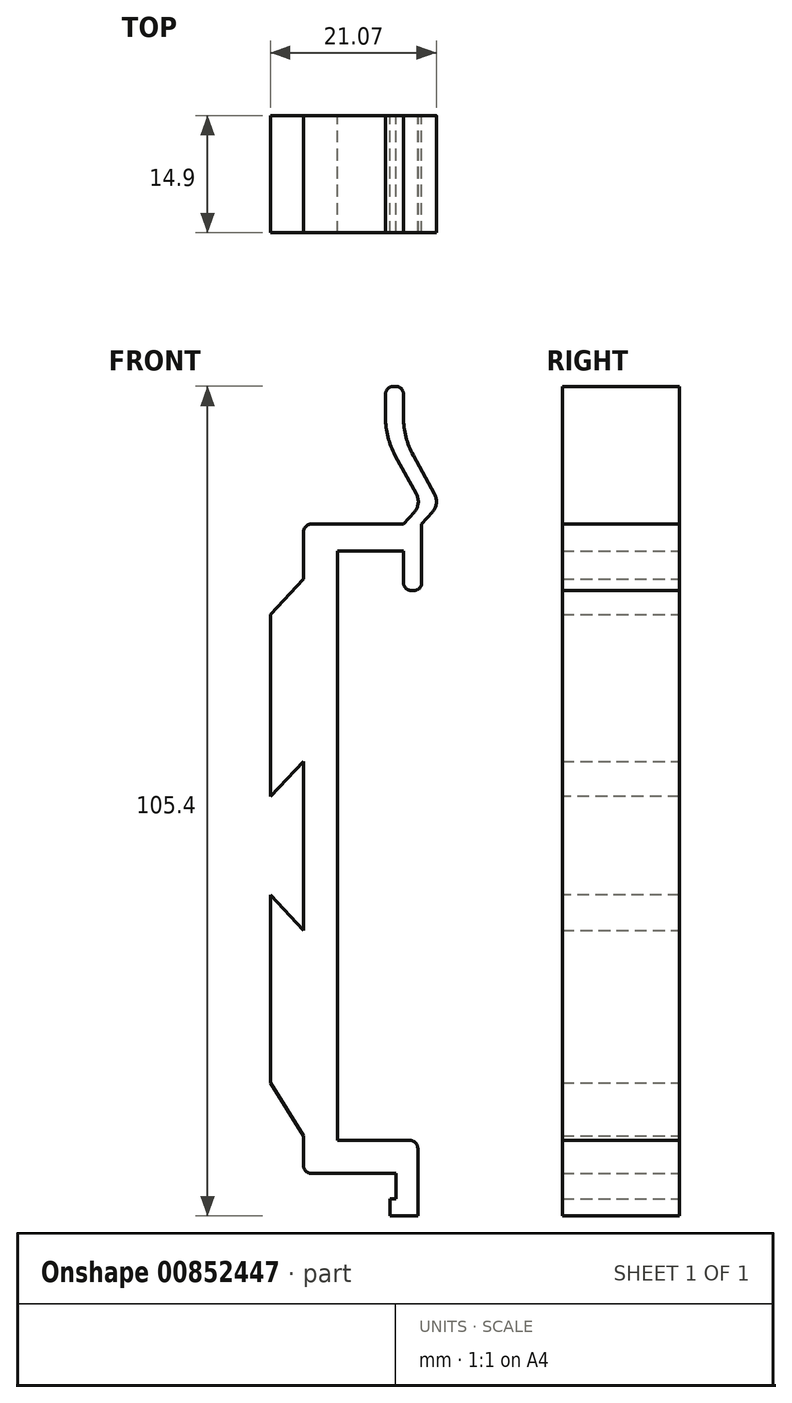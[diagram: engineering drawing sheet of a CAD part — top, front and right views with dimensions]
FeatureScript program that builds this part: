
annotation { "Feature Type Name" : "Feature", "Feature Type Description" : "" }
export const myFeature = defineFeature(function(context is Context, id is Id, definition is map)
    precondition{}
    {
        {
            var Q0;
            Q0=qCreatedBy(makeId("Front.planeOp"),FACE);
            var sketch = newSketch(context, id + "F0", { "sketchPlane" : qUnion([Q0])});
            skLineSegment(sketch, "E0", {"start": v(-4.3, -36.83) * mm, "end": v(-8.5, -30.1) * mm});
            skLineSegment(sketch, "E1", {"start": v(-8.5, -30.1) * mm, "end": v(-8.5, 6.6) * mm});
            skLineSegment(sketch, "E2", {"start": v(-8.5, 6.6) * mm, "end": v(-18.45, 13.87) * mm});
            skLineSegment(sketch, "E3", {"start": v(-18.45, 13.87) * mm, "end": v(-18.45, 27.37) * mm});
            skLineSegment(sketch, "E4", {"start": v(-16.45, 29.37) * mm, "end": v(-13.95, 29.37) * mm});
            skLineSegment(sketch, "E5", {"start": v(-13.95, 29.38) * mm, "end": v(-13.95, 20.08) * mm});
            skLineSegment(sketch, "E6", {"start": v(-13.95, 20.07) * mm, "end": v(-8.5, 20.08) * mm});
            skLineSegment(sketch, "E7", {"start": v(-8.5, 20.08) * mm, "end": v(-8.5, 29.38) * mm});
            skLineSegment(sketch, "E8", {"start": v(-8.5, 29.37) * mm, "end": v(-4.3, 33.87) * mm});
            skLineSegment(sketch, "E9", {"start": v(-4.3, 33.87) * mm, "end": v(-4.3, 39.88) * mm});
            skLineSegment(sketch, "E10", {"start": v(-3.3, 40.88) * mm, "end": v(8.4, 40.88) * mm});
            skLineSegment(sketch, "E11", {"start": v(10.7, 40.88) * mm, "end": v(10.7, 33.43) * mm});
            skLineSegment(sketch, "E12", {"start": v(9.7, 32.43) * mm, "end": v(9.4, 32.43) * mm});
            skLineSegment(sketch, "E13", {"start": v(8.4, 33.43) * mm, "end": v(8.4, 37.43) * mm});
            skLineSegment(sketch, "E14", {"start": v(8.4, 37.43) * mm, "end": v(0, 37.42) * mm});
            skLineSegment(sketch, "E15", {"start": v(0, 37.42) * mm, "end": v(0, -37.42) * mm});
            skLineSegment(sketch, "E16", {"start": v(0, -37.42) * mm, "end": v(9.2, -37.42) * mm});
            skLineSegment(sketch, "E17", {"start": v(10.2, -38.42) * mm, "end": v(10.2, -47.02) * mm});
            skLineSegment(sketch, "E18", {"start": v(10.2, -47.02) * mm, "end": v(6.7, -47.02) * mm});
            skLineSegment(sketch, "E19", {"start": v(6.7, -47.02) * mm, "end": v(6.7, -44.82) * mm});
            skLineSegment(sketch, "E20", {"start": v(6.7, -44.82) * mm, "end": v(7.45, -44.82) * mm});
            skLineSegment(sketch, "E21", {"start": v(7.45, -44.82) * mm, "end": v(7.45, -41.62) * mm});
            skLineSegment(sketch, "E22", {"start": v(7.45, -41.62) * mm, "end": v(-3.3, -41.62) * mm});
            skLineSegment(sketch, "E23", {"start": v(-4.3, -40.62) * mm, "end": v(-4.3, -36.83) * mm});
            skLineSegment(sketch, "E24", {"start": v(8.4, 57.38) * mm, "end": v(8.4, 54.41) * mm});
            skLineSegment(sketch, "E25", {"start": v(9.63, 49.61) * mm, "end": v(12.32, 44.69) * mm});
            skLineSegment(sketch, "E26", {"start": v(12.06, 42.4) * mm, "end": v(10.7, 40.87) * mm});
            skLineSegment(sketch, "E27", {"start": v(7.4, 58.38) * mm, "end": v(7.1, 58.38) * mm});
            skLineSegment(sketch, "E28", {"start": v(6.1, 57.38) * mm, "end": v(6.1, 54.41) * mm});
            skLineSegment(sketch, "E29", {"start": v(7.33, 49.61) * mm, "end": v(10.02, 44.69) * mm});
            skLineSegment(sketch, "E30", {"start": v(9.76, 42.4) * mm, "end": v(8.4, 40.88) * mm});
            skPoint(sketch, "E31.visualSharp", {"position": v(6.1, 51.86) * mm});
            skArc(sketch, "E31.filletArc", {"start": v(6.1, 54.41) * mm, "mid": v(6.41, 51.94) * mm, "end": v(7.33, 49.61) * mm});
            skPoint(sketch, "E32.visualSharp", {"position": v(8.4, 51.86) * mm});
            skArc(sketch, "E32.filletArc", {"start": v(8.4, 54.41) * mm, "mid": v(8.71, 51.94) * mm, "end": v(9.63, 49.61) * mm});
            skPoint(sketch, "E33.visualSharp", {"position": v(10.7, 43.45) * mm});
            skArc(sketch, "E33.filletArc", {"start": v(9.76, 42.4) * mm, "mid": v(10.25, 43.5) * mm, "end": v(10.02, 44.69) * mm});
            skPoint(sketch, "E34.visualSharp", {"position": v(13, 43.45) * mm});
            skArc(sketch, "E34.filletArc", {"start": v(12.06, 42.4) * mm, "mid": v(12.55, 43.5) * mm, "end": v(12.32, 44.69) * mm});
            skPoint(sketch, "E35.visualSharp", {"position": v(8.4, 58.38) * mm});
            skArc(sketch, "E35.filletArc", {"start": v(8.4, 57.38) * mm, "mid": v(8.1, 58.08) * mm, "end": v(7.4, 58.38) * mm});
            skPoint(sketch, "E36.visualSharp", {"position": v(6.1, 58.38) * mm});
            skArc(sketch, "E36.filletArc", {"start": v(7.1, 58.38) * mm, "mid": v(6.4, 58.08) * mm, "end": v(6.1, 57.38) * mm});
            skPoint(sketch, "E37.visualSharp", {"position": v(10.7, 32.43) * mm});
            skArc(sketch, "E37.filletArc", {"start": v(9.7, 32.43) * mm, "mid": v(10.4, 32.72) * mm, "end": v(10.7, 33.43) * mm});
            skPoint(sketch, "E38.visualSharp", {"position": v(8.4, 32.43) * mm});
            skArc(sketch, "E38.filletArc", {"start": v(8.4, 33.43) * mm, "mid": v(8.7, 32.72) * mm, "end": v(9.4, 32.43) * mm});
            skPoint(sketch, "E39.visualSharp", {"position": v(-4.3, 40.87) * mm});
            skArc(sketch, "E39.filletArc", {"start": v(-3.3, 40.88) * mm, "mid": v(-4, 40.58) * mm, "end": v(-4.3, 39.88) * mm});
            skPoint(sketch, "E40.visualSharp", {"position": v(-18.45, 29.37) * mm});
            skArc(sketch, "E40.filletArc", {"start": v(-16.45, 29.38) * mm, "mid": v(-17.86, 28.79) * mm, "end": v(-18.45, 27.37) * mm});
            skPoint(sketch, "E41.visualSharp", {"position": v(-4.3, -41.62) * mm});
            skArc(sketch, "E41.filletArc", {"start": v(-4.3, -40.62) * mm, "mid": v(-4, -41.33) * mm, "end": v(-3.3, -41.62) * mm});
            skPoint(sketch, "E42.visualSharp", {"position": v(10.2, -37.42) * mm});
            skArc(sketch, "E42.filletArc", {"start": v(10.2, -38.42) * mm, "mid": v(9.9, -37.72) * mm, "end": v(9.2, -37.42) * mm});
            skSolve(sketch);
        }
        {
            var Q0;
            Q0=qSketchRegion(id+"F0",true);
            extrude(context, id + "F1", {"entities" : qUnion([Q0]), "depth" : 14.9 * mm, "symmetric" : true});
        }
        {
            var Q0;
            Q0=makeQuery(id+"F1.opExtrude","CAP_FACE",FACE,{"disambiguationData":[OSD([sQuery(id+"F0.wireOp",EDGE,"E0"),sQuery(id+"F0.wireOp",EDGE,"E1"),sQuery(id+"F0.wireOp",EDGE,"E2"),sQuery(id+"F0.wireOp",EDGE,"E3"),sQuery(id+"F0.wireOp",EDGE,"E4"),sQuery(id+"F0.wireOp",EDGE,"E5"),sQuery(id+"F0.wireOp",EDGE,"E6"),sQuery(id+"F0.wireOp",EDGE,"E7"),sQuery(id+"F0.wireOp",EDGE,"E8"),sQuery(id+"F0.wireOp",EDGE,"E9"),sQuery(id+"F0.wireOp",EDGE,"E10"),sQuery(id+"F0.wireOp",EDGE,"E11"),sQuery(id+"F0.wireOp",EDGE,"E12"),sQuery(id+"F0.wireOp",EDGE,"E13"),sQuery(id+"F0.wireOp",EDGE,"E14"),sQuery(id+"F0.wireOp",EDGE,"E15"),sQuery(id+"F0.wireOp",EDGE,"E16"),sQuery(id+"F0.wireOp",EDGE,"E17"),sQuery(id+"F0.wireOp",EDGE,"E18"),sQuery(id+"F0.wireOp",EDGE,"E19"),sQuery(id+"F0.wireOp",EDGE,"E20"),sQuery(id+"F0.wireOp",EDGE,"E21"),sQuery(id+"F0.wireOp",EDGE,"E22"),sQuery(id+"F0.wireOp",EDGE,"E23"),sQuery(id+"F0.wireOp",EDGE,"E24"),sQuery(id+"F0.wireOp",EDGE,"E25"),sQuery(id+"F0.wireOp",EDGE,"E26"),sQuery(id+"F0.wireOp",EDGE,"E27"),sQuery(id+"F0.wireOp",EDGE,"E28"),sQuery(id+"F0.wireOp",EDGE,"E29"),sQuery(id+"F0.wireOp",EDGE,"E30"),sQuery(id+"F0.wireOp",EDGE,"E31.filletArc"),sQuery(id+"F0.wireOp",EDGE,"E32.filletArc"),sQuery(id+"F0.wireOp",EDGE,"E33.filletArc"),sQuery(id+"F0.wireOp",EDGE,"E34.filletArc"),sQuery(id+"F0.wireOp",EDGE,"E35.filletArc"),sQuery(id+"F0.wireOp",EDGE,"E36.filletArc"),sQuery(id+"F0.wireOp",EDGE,"E37.filletArc"),sQuery(id+"F0.wireOp",EDGE,"E38.filletArc"),sQuery(id+"F0.wireOp",EDGE,"E39.filletArc"),sQuery(id+"F0.wireOp",EDGE,"E40.filletArc"),sQuery(id+"F0.wireOp",EDGE,"E41.filletArc"),sQuery(id+"F0.wireOp",EDGE,"E42.filletArc")])],"isStart":false});
            var sketch = newSketch(context, id + "F2", { "sketchPlane" : qUnion([Q0])});
            skLineSegment(sketch, "E43.bottom", {"start": v(-18.45, 29.38) * mm, "end": v(-8.5, 29.38) * mm});
            skLineSegment(sketch, "E43.top", {"start": v(-18.45, -30.1) * mm, "end": v(-8.5, -30.1) * mm});
            skLineSegment(sketch, "E43.left", {"start": v(-18.45, 29.38) * mm, "end": v(-18.45, -30.1) * mm});
            skLineSegment(sketch, "E43.right", {"start": v(-8.5, 29.38) * mm, "end": v(-8.5, -30.1) * mm});
            skSolve(sketch);
        }
        {
            var Q0;
            Q0 = qSketchRegion(id + "F2", true);
            extrude(context, id + "F3", {"entities" : qUnion([Q0]), "operationType" : NewBodyOperationType.REMOVE, "endBound" : BoundingType.THROUGH_ALL, "oppositeDirection" : true, "depth" : 25 * mm, "offsetDistance" : 25 * mm});
        }
        {
            var Q0;
            Q0=makeQuery(id+"F1.opExtrude","CAP_FACE",FACE,{"disambiguationData":[OSD([sQuery(id+"F0.wireOp",EDGE,"E0"),sQuery(id+"F0.wireOp",EDGE,"E1"),sQuery(id+"F0.wireOp",EDGE,"E2"),sQuery(id+"F0.wireOp",EDGE,"E3"),sQuery(id+"F0.wireOp",EDGE,"E4"),sQuery(id+"F0.wireOp",EDGE,"E5"),sQuery(id+"F0.wireOp",EDGE,"E6"),sQuery(id+"F0.wireOp",EDGE,"E7"),sQuery(id+"F0.wireOp",EDGE,"E8"),sQuery(id+"F0.wireOp",EDGE,"E9"),sQuery(id+"F0.wireOp",EDGE,"E10"),sQuery(id+"F0.wireOp",EDGE,"E11"),sQuery(id+"F0.wireOp",EDGE,"E12"),sQuery(id+"F0.wireOp",EDGE,"E13"),sQuery(id+"F0.wireOp",EDGE,"E14"),sQuery(id+"F0.wireOp",EDGE,"E15"),sQuery(id+"F0.wireOp",EDGE,"E16"),sQuery(id+"F0.wireOp",EDGE,"E17"),sQuery(id+"F0.wireOp",EDGE,"E18"),sQuery(id+"F0.wireOp",EDGE,"E19"),sQuery(id+"F0.wireOp",EDGE,"E20"),sQuery(id+"F0.wireOp",EDGE,"E21"),sQuery(id+"F0.wireOp",EDGE,"E22"),sQuery(id+"F0.wireOp",EDGE,"E23"),sQuery(id+"F0.wireOp",EDGE,"E24"),sQuery(id+"F0.wireOp",EDGE,"E25"),sQuery(id+"F0.wireOp",EDGE,"E26"),sQuery(id+"F0.wireOp",EDGE,"E27"),sQuery(id+"F0.wireOp",EDGE,"E28"),sQuery(id+"F0.wireOp",EDGE,"E29"),sQuery(id+"F0.wireOp",EDGE,"E30"),sQuery(id+"F0.wireOp",EDGE,"E31.filletArc"),sQuery(id+"F0.wireOp",EDGE,"E32.filletArc"),sQuery(id+"F0.wireOp",EDGE,"E33.filletArc"),sQuery(id+"F0.wireOp",EDGE,"E34.filletArc"),sQuery(id+"F0.wireOp",EDGE,"E35.filletArc"),sQuery(id+"F0.wireOp",EDGE,"E36.filletArc"),sQuery(id+"F0.wireOp",EDGE,"E37.filletArc"),sQuery(id+"F0.wireOp",EDGE,"E38.filletArc"),sQuery(id+"F0.wireOp",EDGE,"E39.filletArc"),sQuery(id+"F0.wireOp",EDGE,"E40.filletArc"),sQuery(id+"F0.wireOp",EDGE,"E41.filletArc"),sQuery(id+"F0.wireOp",EDGE,"E42.filletArc")])],"isStart":true});
            var sketch = newSketch(context, id + "F4", { "sketchPlane" : qUnion([Q0])});
            skLineSegment(sketch, "E44", {"start": v(10, 4.64) * mm, "end": v(4.3, 10.75) * mm});
            skLineSegment(sketch, "E45", {"start": v(4.3, 10.75) * mm, "end": v(4.3, 0) * mm});
            skLineSegment(sketch, "E46", {"start": v(13.6, 0) * mm, "end": v(-4.27, 0) * mm, "construction": true});
            skLineSegment(sketch, "E47.MirrorCS", {"start": v(4.3, -10.75) * mm, "end": v(4.3, 0) * mm});
            skLineSegment(sketch, "E48.MirrorCS", {"start": v(10, -4.64) * mm, "end": v(4.3, -10.75) * mm});
            skLineSegment(sketch, "E49", {"start": v(10, -4.64) * mm, "end": v(10, 4.64) * mm});
            skSolve(sketch);
        }
        {
            var Q0;
            Q0 = qSketchRegion(id + "F4", true);
            extrude(context, id + "F5", {"entities" : qUnion([Q0]), "operationType" : NewBodyOperationType.REMOVE, "endBound" : BoundingType.UP_TO_NEXT, "oppositeDirection" : true, "depth" : 25 * mm, "offsetDistance" : 25 * mm});
        }
    });
